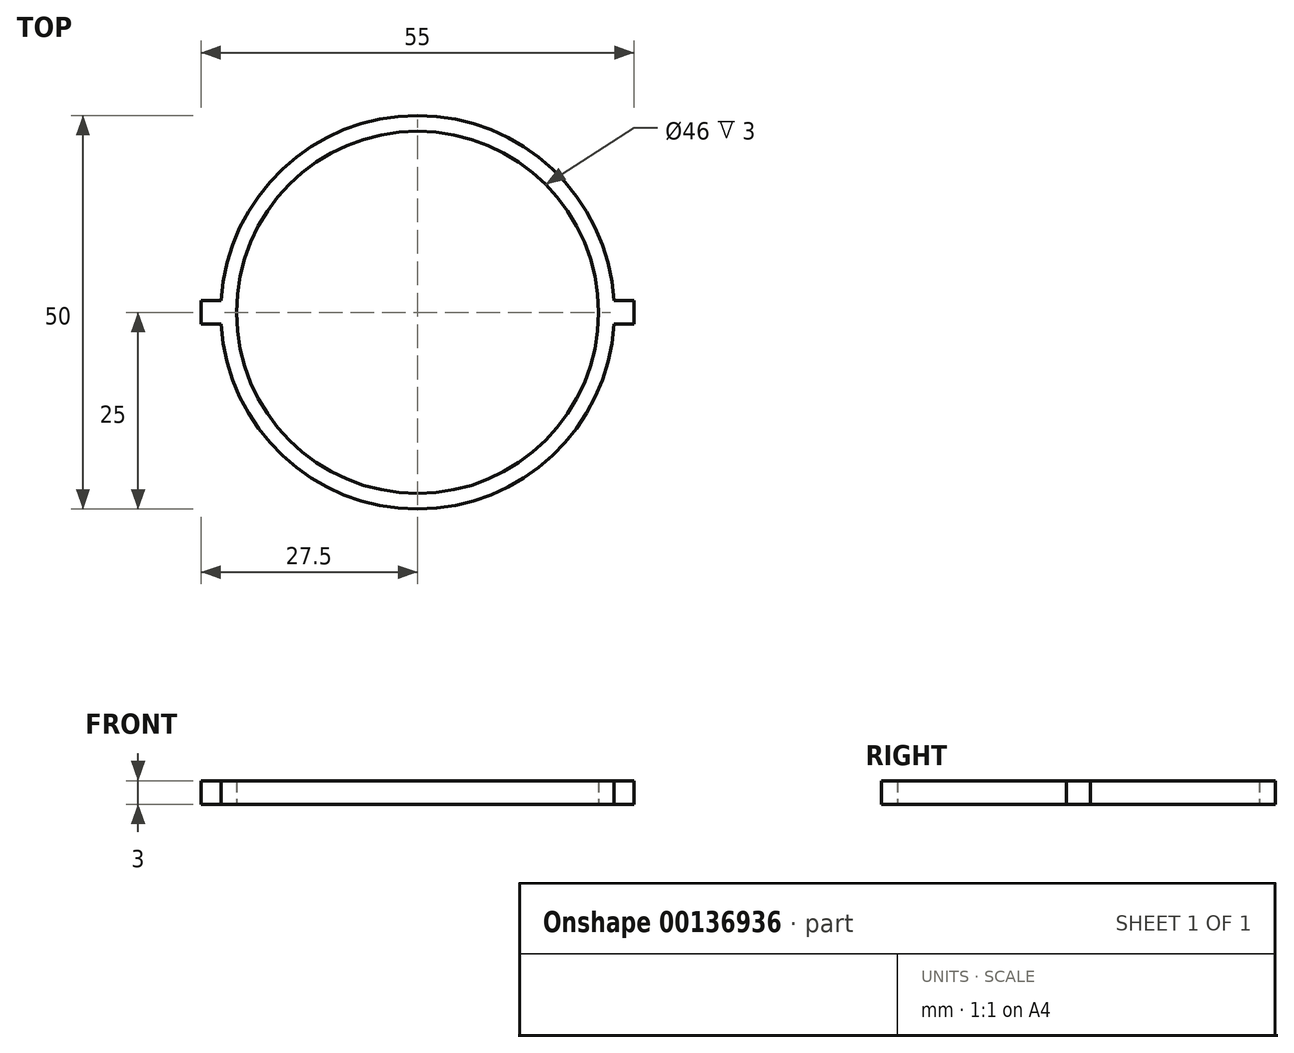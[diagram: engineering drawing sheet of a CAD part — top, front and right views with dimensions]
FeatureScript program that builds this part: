
annotation { "Feature Type Name" : "Feature", "Feature Type Description" : "" }
export const myFeature = defineFeature(function(context is Context, id is Id, definition is map)
    precondition{}
    {
        {
            var Q0;
            Q0=qCreatedBy(makeId("Top.planeOp"),FACE);
            var sketch = newSketch(context, id + "F0", { "sketchPlane" : qUnion([Q0])});
            skCircle(sketch, "E0", {"center": v(0, 0) * mm, "radius": 25 * mm});
            skCircle(sketch, "E1", {"center": v(0, 0) * mm, "radius": 23 * mm});
            skLineSegment(sketch, "E2.bottom", {"start": v(-27.5, -1.5) * mm, "end": v(27.5, -1.5) * mm});
            skLineSegment(sketch, "E2.top", {"start": v(-27.5, 1.5) * mm, "end": v(27.5, 1.5) * mm});
            skLineSegment(sketch, "E2.left", {"start": v(-27.5, -1.5) * mm, "end": v(-27.5, 1.5) * mm});
            skLineSegment(sketch, "E2.right", {"start": v(27.5, -1.5) * mm, "end": v(27.5, 1.5) * mm});
            skSolve(sketch);
        }
        {
            var Q0;
            Q0=makeQuery(id+"F0.imprint","IMPRINT",FACE,{"disambiguationData":[TD([[makeQuery(id+"F0.imprint","IMPRINT",EDGE,{"derivedFrom":sQuery(id+"F0.wireOp",EDGE,"E0")}),1.0]])]});
            var Q1;
            {var subQ5=sQuery(id+"F0.wireOp",EDGE,"E2.right");Q1=makeQuery(id+"F0.imprint","IMPRINT",FACE,{"disambiguationData":[TD([[makeQuery(id+"F0.imprint","IMPRINT",EDGE,{"derivedFrom":subQ5}),1.0]])]});}
            var Q2;
            {var subQ5=sQuery(id+"F0.wireOp",EDGE,"E2.left");Q2=makeQuery(id+"F0.imprint","IMPRINT",FACE,{"disambiguationData":[TD([[makeQuery(id+"F0.imprint","IMPRINT",EDGE,{"derivedFrom":subQ5}),-1.0]])]});}
            extrude(context, id + "F1", {"entities" : qUnion([Q0, Q1, Q2]), "depth" : 3 * mm});
        }
    });
